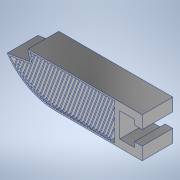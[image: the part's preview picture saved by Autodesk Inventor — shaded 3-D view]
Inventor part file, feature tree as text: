
AUTODESK INVENTOR PART (.ipt)
format: ipt  version: 2022 (Build 260153000, 153)  size: 560,640 bytes
history: native  units: mm
features: extrude x7, sketch x6, fillet x1, shell x1, projected_geometry x1
ambient origin geometry x8: Origin, YZ Plane, XZ Plane, XY Plane, X Axis, Y Axis, Z Axis, Center Point
bodies: Body1 (feature_tree)
feature tree (16):
  extrude  "Extrusion2"  Depth=5.8mm
  extrude  "Extrusion5"  Depth=12.0mm TaperAngle=0.0deg
  fillet  "Fillet2"  Radius=45.0mm
  shell  "Shell1"  Thickness=15.6mm
  extrude  "Extrusion7"  TaperAngle=0.0deg  [1 undecoded]
  extrude  "Extrusion8"  Depth=9.6mm
  extrude  "Extrusion9"  Depth=9.0mm
  extrude  "Extrusion10"  Depth=23.0mm
  extrude  "Extrusion11"  Depth=0.62mm
  sketch  "Sketch8"  dims[d41=5.8mm d48=44.0mm]
  sketch  "Sketch13"  dims[d50=3.0mm d56=12.0mm d57=0.0mm d63=45.0mm d67=15.6mm d71=0.0mm]
  sketch  "Sketch14"  dims[d80=17.453293mm d82=0.0mm d83=0.0mm]
  projected_geometry  "Projected Loop1"
  sketch  "Sketch15"  dims[d87=5.6mm d88=9.6mm]
  sketch  "Sketch16"  dims[d95=4.0mm d96=9.0mm]
  sketch  "Sketch17"  dims[d97=15.6mm d98=23.0mm d99=0.62mm d100=12.0mm d101=0.0mm d102=10.747401mm d103=12.0mm d104=0.0mm d105=0.38mm d107=0.38mm d1=0.38mm d110=0.38mm d111=0.38mm d112=0.38mm d113=0.38mm d127=12.0mm d128=0.0mm d129=0.38mm d131=0.38mm d132=0.38mm d133=0.38mm d134=0.38mm d135=0.38mm d136=0.38mm d137=0.38mm d138=0.38mm d139=0.38mm d151=0.38mm d157=0.38mm d161=0.38mm d163=0.38mm d168=0.89mm d169=0.38mm d170=0.89mm d171=0.89mm d172=0.38mm d173=0.89mm d174=0.89mm d175=0.38mm d176=0.89mm d178=0.38mm d179=0.89mm d182=0.89mm d184=0.89mm d185=19.198622mm d186=19.198622mm d187=19.198622mm d189=0.89mm d193=0.89mm d194=0.89mm d195=0.89mm d196=0.89mm d197=0.89mm d200=0.38mm d201=19.198622mm d202=0.89mm d205=0.89mm d206=0.89mm d207=0.89mm d209=0.89mm d210=0.38mm d211=0.38mm d213=0.89mm d214=0.38mm d215=0.38mm d216=0.38mm d217=0.89mm d218=0.89mm d219=12.0mm d220=0.0mm d221=0.89mm d222=0.89mm d223=0.89mm d224=0.38mm d225=0.89mm d226=0.89mm d227=0.89mm d228=0.89mm d229=0.89mm d230=12.0mm d231=0.0mm]
note: 1 required parameter value undecoded (feature->parameter linkage not recoverable at this tier; creation-order binding heuristic only, values carry confidence <= 0.55)
